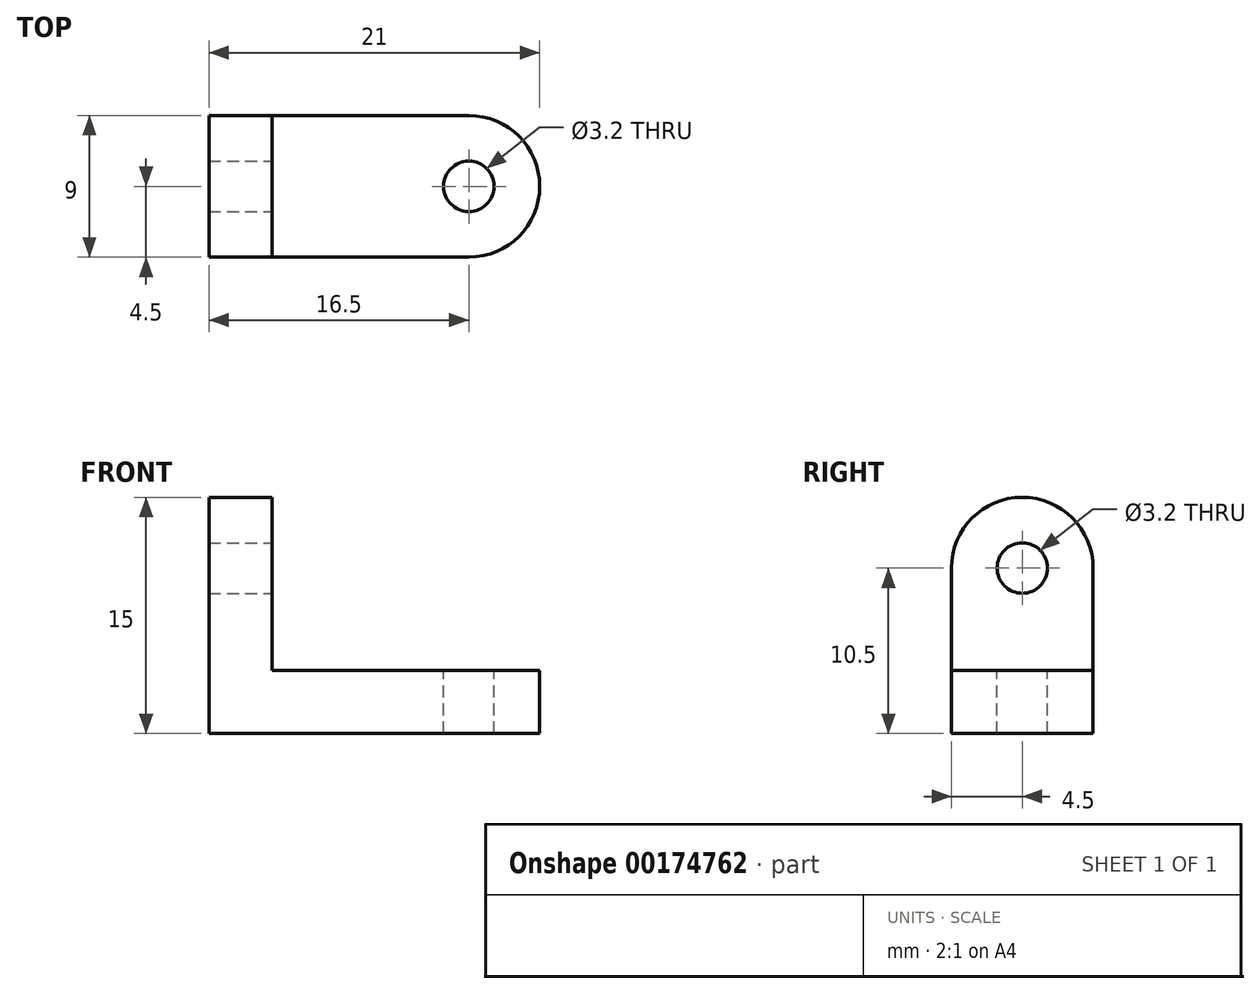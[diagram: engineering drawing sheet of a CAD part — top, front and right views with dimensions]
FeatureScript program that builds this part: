
annotation { "Feature Type Name" : "Feature", "Feature Type Description" : "" }
export const myFeature = defineFeature(function(context is Context, id is Id, definition is map)
    precondition{}
    {
        {
            var Q0;
            Q0=qCreatedBy(makeId("Front.planeOp"),FACE);
            var sketch = newSketch(context, id + "F0", { "sketchPlane" : qUnion([Q0])});
            skLineSegment(sketch, "E0", {"start": v(-15, 0) * mm, "end": v(0, 0) * mm});
            skLineSegment(sketch, "E1", {"start": v(0, 0) * mm, "end": v(0, 21) * mm});
            skLineSegment(sketch, "E2.0", {"start": v(-4, 4) * mm, "end": v(-4, 21) * mm});
            skLineSegment(sketch, "E2.1", {"start": v(-15, 4) * mm, "end": v(-4, 4) * mm});
            skLineSegment(sketch, "E3", {"start": v(-15, 4) * mm, "end": v(-15, 0) * mm});
            skLineSegment(sketch, "E4", {"start": v(-4, 21) * mm, "end": v(0, 21) * mm});
            skSolve(sketch);
        }
        {
            var Q0;
            Q0 = qSketchRegion(id + "F0", true);
            extrude(context, id + "F1", {"entities" : qUnion([Q0]), "depth" : 9 * mm});
        }
        {
            var Q0;
            Q0=makeQuery(id+"F1.opExtrude","SWEPT_FACE",FACE,{"disambiguationData":[OSD([sQuery(id+"F0.wireOp",EDGE,"E2.1")])]});
            var sketch = newSketch(context, id + "F2", { "sketchPlane" : qUnion([Q0])});
            skCircle(sketch, "E5", {"center": v(-10.5, -4.5) * mm, "radius": 1.6 * mm});
            skPoint(sketch, "E5.centerSnap0", {"position": v(-15, -4.5) * mm});
            skSolve(sketch);
        }
        {
            var Q0;
            Q0 = qSketchRegion(id + "F2", true);
            extrude(context, id + "F3", {"entities" : qUnion([Q0]), "operationType" : NewBodyOperationType.REMOVE, "oppositeDirection" : true, "depth" : 25 * mm});
        }
        {
            var Q0;
            Q0=makeQuery(id+"F1.opExtrude","SWEPT_FACE",FACE,{"disambiguationData":[OSD([sQuery(id+"F0.wireOp",EDGE,"E2.0")])]});
            var sketch = newSketch(context, id + "F4", { "sketchPlane" : qUnion([Q0])});
            skCircle(sketch, "E6", {"center": v(4.5, 16.5) * mm, "radius": 1.6 * mm});
            skPoint(sketch, "E6.centerSnap0", {"position": v(4.5, 21) * mm});
            skSolve(sketch);
        }
        {
            var Q0;
            Q0 = qSketchRegion(id + "F4", true);
            extrude(context, id + "F5", {"entities" : qUnion([Q0]), "operationType" : NewBodyOperationType.REMOVE, "oppositeDirection" : true, "depth" : 25 * mm});
        }
        {
            var Q0;
            Q0=makeQuery(id+"F1.opExtrude","CAP_EDGE",EDGE,{"disambiguationData":[OSD([sQuery(id+"F0.wireOp",EDGE,"E4")])],"isStart":false});
            var Q1;
            Q1=makeQuery(id+"F1.opExtrude","CAP_EDGE",EDGE,{"disambiguationData":[OSD([sQuery(id+"F0.wireOp",EDGE,"E4")])],"isStart":true});
            var Q2;
            Q2=makeQuery(id+"F1.opExtrude","CAP_EDGE",EDGE,{"disambiguationData":[OSD([sQuery(id+"F0.wireOp",EDGE,"E3")])],"isStart":true});
            var Q3;
            Q3=makeQuery(id+"F1.opExtrude","CAP_EDGE",EDGE,{"disambiguationData":[OSD([sQuery(id+"F0.wireOp",EDGE,"E3")])],"isStart":false});
            fillet(context, id + "F6", {"entities" : qUnion([Q0, Q1, Q2, Q3]), "radius" : 4.5 * mm, "tangentPropagation" : true, "allowEdgeOverflow" : false});
        }
        {
            var Q0;
            Q0=makeQuery(id+"F1.opExtrude","SWEPT_BODY",BODY,{"disambiguationData":[OSD([sQuery(id+"F0.wireOp",EDGE,"E0"),sQuery(id+"F0.wireOp",EDGE,"E1"),sQuery(id+"F0.wireOp",EDGE,"E2.0"),sQuery(id+"F0.wireOp",EDGE,"E2.1"),sQuery(id+"F0.wireOp",EDGE,"E3"),sQuery(id+"F0.wireOp",EDGE,"E4")])]});
            var Q1;
            Q1=makeQuery(id+"F1.opExtrude","SWEPT_EDGE",EDGE,{"disambiguationData":[OSD([sQuery(id+"F0.wireOp",EDGE,"E0"),sQuery(id+"F0.wireOp",EDGE,"E1")])]});
            transform(context, id + "F7", {"entities" : qUnion([Q0]), "transformType" : TransformType.ROTATION, "transformAxis" : qUnion([Q1]), "angle" : 90 * degree, "makeCopy" : false});
        }
    });
